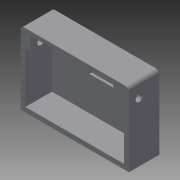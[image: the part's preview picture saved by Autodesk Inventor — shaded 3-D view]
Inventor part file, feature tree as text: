
AUTODESK INVENTOR PART (.ipt)
format: ipt  version: 2014 (Build 180170000, 170)  size: 150,528 bytes
history: native  units: in
note: dims shown in document units (in); Inventor stores cm internally (conversion verified against a paired STEP export)
features: extrude x5, sketch x5, chamfer x2, fillet x2, hole x1, projected_geometry x1
ambient origin geometry x8: Origin, YZ Plane, XZ Plane, XY Plane, X Axis, Y Axis, Z Axis, Center Point
bodies: Solid1 (feature_tree)
feature tree (16):
  extrude  "Extrusion1"  Depth=1.82in
  extrude  "Extrusion2"  Depth=2.46in
  chamfer  "Chamfer1"  Distance=0.12in
  chamfer  "Chamfer2"  Distance=0.12in
  extrude  "Extrusion3"  TaperAngle=0.0deg  [1 undecoded]
  extrude  "Extrusion4"  Depth=0.25in
  fillet  "Fillet1"  Radius=0.66in
  fillet  "Fillet2"  Radius=0.25in
  extrude  "Extrusion5"  Depth=0.25in TaperAngle=45.0deg
  hole  "Hole1"  [1 undecoded]
  sketch  "Sketch1"  dims[d0=2.7in d1=1.82in]
  sketch  "Sketch2"  dims[d2=0.1in d3=0.0in d4=2.46in]
  sketch  "Sketch3"  dims[d5=2.1in]
  projected_geometry  "Projected Loop1"
  sketch  "Sketch4"  dims[d6=0.6in]
  sketch  "Sketch5"  dims[d7=1.0in d8=0.12in d9=0.12in d10=0.0in d13=0.25in d14=0.66in d15=0.0in d16=0.25in d17=0.5in d18=45.0deg d19=0.25in d20=0.5in d21=45.0deg d22=0.4in d23=1.35in d24=0.275in d25=0.66in d26=0.0in d27=0.116in d28=0.3in d29=0.59in d30=0.3in d31=0.0in d32=0.058in d33=0.1in d34=0.75in d35=0.6in d36=0.3in d37=0.3in d38=0.06in d39=0.0in d40=0.25in d41=0.25in d42=0.164in d43=0.75in d44=0.375in d45=0.25in d46=0.5635in d47=1.0in d48=0.8108in]
note: 2 required parameter values undecoded (feature->parameter linkage not recoverable at this tier; creation-order binding heuristic only, values carry confidence <= 0.55)
